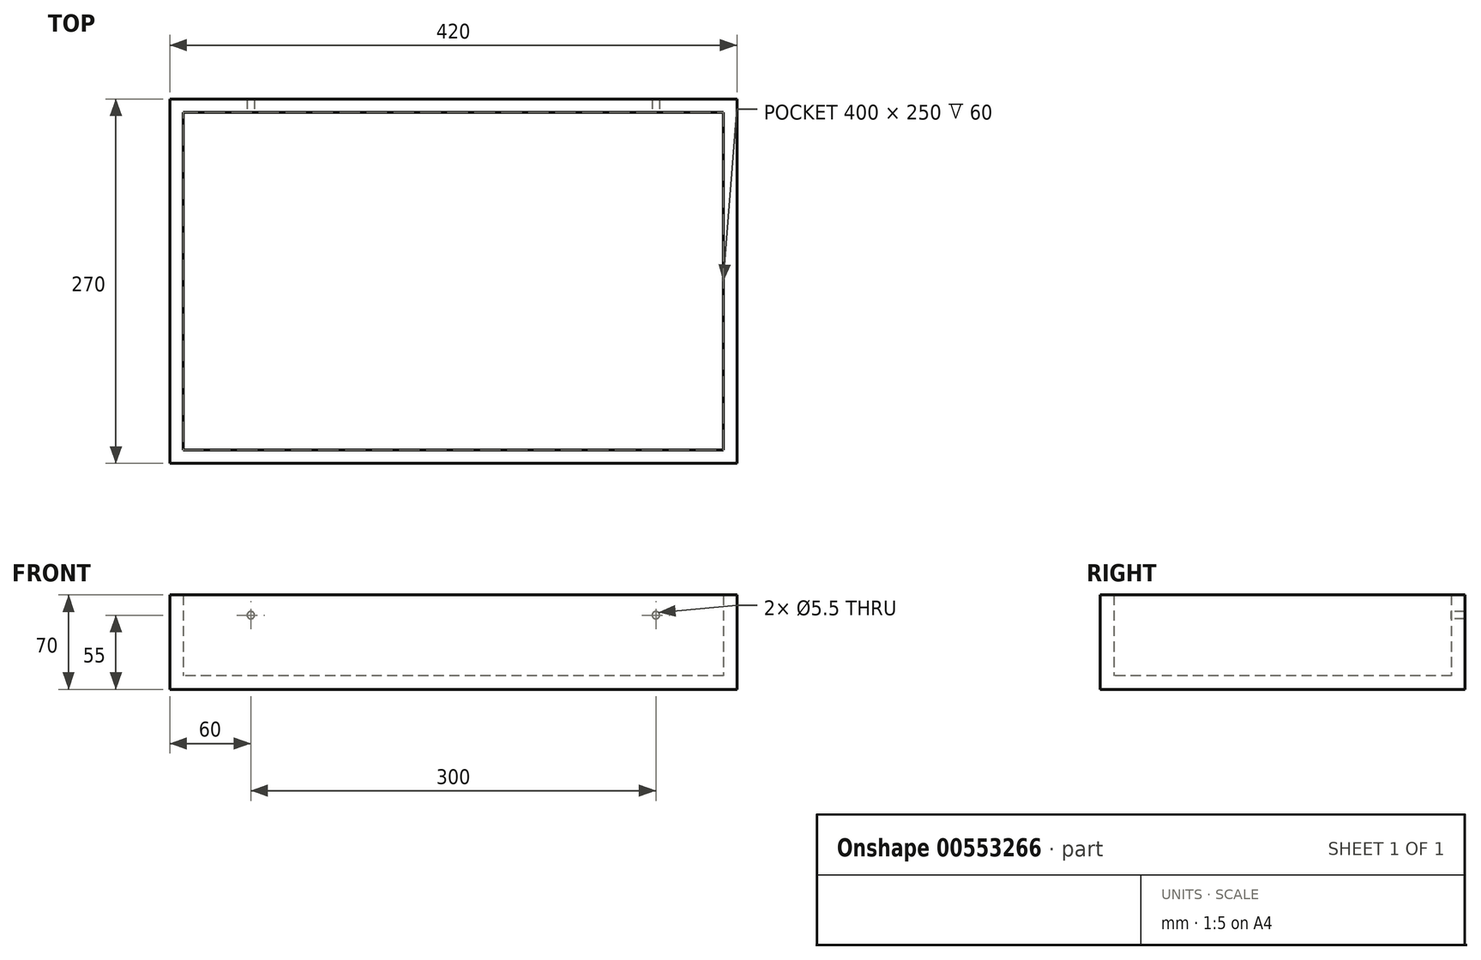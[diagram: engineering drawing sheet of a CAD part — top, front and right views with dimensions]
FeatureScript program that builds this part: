
annotation { "Feature Type Name" : "Feature", "Feature Type Description" : "" }
export const myFeature = defineFeature(function(context is Context, id is Id, definition is map)
    precondition{}
    {
        {
            var Q0;
            Q0=qCreatedBy(makeId("Top.planeOp"),FACE);
            var sketch = newSketch(context, id + "F0", { "sketchPlane" : qUnion([Q0])});
            skLineSegment(sketch, "E0.bottom", {"start": v(200, 125) * mm, "end": v(-200, 125) * mm});
            skLineSegment(sketch, "E0.top", {"start": v(200, -125) * mm, "end": v(-200, -125) * mm});
            skLineSegment(sketch, "E0.left", {"start": v(200, 125) * mm, "end": v(200, -125) * mm});
            skLineSegment(sketch, "E0.right", {"start": v(-200, 125) * mm, "end": v(-200, -125) * mm});
            skPoint(sketch, "E0.middle", {"position": v(0, 0) * mm});
            skSolve(sketch);
        }
        {
            var Q0;
            Q0 = qSketchRegion(id + "F0", true);
            extrude(context, id + "F1", {"entities" : qUnion([Q0]), "depth" : 10 * mm, "offsetDistance" : 25 * mm});
        }
        {
            var Q0;
            Q0=makeQuery(id+"F1.opExtrude","SWEPT_FACE",FACE,{"disambiguationData":[OSD([sQuery(id+"F0.wireOp",EDGE,"E0.left")])]});
            var sketch = newSketch(context, id + "F2", { "sketchPlane" : qUnion([Q0])});
            skLineSegment(sketch, "E1.bottom", {"start": v(-125, 0) * mm, "end": v(125, 0) * mm});
            skLineSegment(sketch, "E1.top", {"start": v(-125, 70) * mm, "end": v(125, 70) * mm});
            skLineSegment(sketch, "E1.left", {"start": v(-125, 0) * mm, "end": v(-125, 70) * mm});
            skLineSegment(sketch, "E1.right", {"start": v(125, 0) * mm, "end": v(125, 70) * mm});
            skSolve(sketch);
        }
        {
            var Q0;
            Q0 = qSketchRegion(id + "F2", true);
            extrude(context, id + "F3", {"entities" : qUnion([Q0]), "operationType" : NewBodyOperationType.ADD, "depth" : 10 * mm, "offsetDistance" : 25 * mm});
        }
        {
            var Q0;
            Q0=makeQuery(id+"F3.boolean.opBoolean","MERGE",FACE,{"derivedFrom":[makeQuery(id+"F1.opExtrude","SWEPT_FACE",FACE,{"disambiguationData":[OSD([sQuery(id+"F0.wireOp",EDGE,"E0.bottom")])]}),makeQuery(id+"F3.opExtrude","SWEPT_FACE",FACE,{"disambiguationData":[OSD([sQuery(id+"F2.wireOp",EDGE,"E1.right")])]})]});
            var sketch = newSketch(context, id + "F4", { "sketchPlane" : qUnion([Q0])});
            skLineSegment(sketch, "E2.bottom", {"start": v(-210, 0) * mm, "end": v(210, 0) * mm});
            skLineSegment(sketch, "E2.top", {"start": v(-210, 70) * mm, "end": v(210, 70) * mm});
            skLineSegment(sketch, "E2.left", {"start": v(-210, 0) * mm, "end": v(-210, 70) * mm});
            skLineSegment(sketch, "E2.right", {"start": v(210, 0) * mm, "end": v(210, 70) * mm});
            skPoint(sketch, "E3", {"position": v(-150, 55) * mm});
            skPoint(sketch, "E4", {"position": v(150, 55) * mm});
            skSolve(sketch);
        }
        {
            var Q0;
            Q0 = qSketchRegion(id + "F4", true);
            extrude(context, id + "F5", {"entities" : qUnion([Q0]), "operationType" : NewBodyOperationType.ADD, "depth" : 10 * mm, "offsetDistance" : 25 * mm});
        }
        {
            var Q0;
            Q0=makeQuery(id+"F1.opExtrude","SWEPT_FACE",FACE,{"disambiguationData":[OSD([sQuery(id+"F0.wireOp",EDGE,"E0.right")])]});
            var sketch = newSketch(context, id + "F6", { "sketchPlane" : qUnion([Q0])});
            skLineSegment(sketch, "E5.bottom", {"start": v(-125, 0) * mm, "end": v(125, 0) * mm});
            skLineSegment(sketch, "E5.top", {"start": v(-125, 70) * mm, "end": v(125, 70) * mm});
            skLineSegment(sketch, "E5.left", {"start": v(-125, 0) * mm, "end": v(-125, 70) * mm});
            skLineSegment(sketch, "E5.right", {"start": v(125, 0) * mm, "end": v(125, 70) * mm});
            skSolve(sketch);
        }
        {
            var Q0;
            Q0 = qSketchRegion(id + "F6", true);
            extrude(context, id + "F7", {"entities" : qUnion([Q0]), "operationType" : NewBodyOperationType.ADD, "depth" : 10 * mm, "offsetDistance" : 25 * mm});
        }
        {
            var Q0;
            Q0=makeQuery(id+"F7.boolean.opBoolean","MERGE",FACE,{"derivedFrom":[makeQuery(id+"F3.boolean.opBoolean","MERGE",FACE,{"derivedFrom":[makeQuery(id+"F1.opExtrude","SWEPT_FACE",FACE,{"disambiguationData":[OSD([sQuery(id+"F0.wireOp",EDGE,"E0.top")])]}),makeQuery(id+"F3.opExtrude","SWEPT_FACE",FACE,{"disambiguationData":[OSD([sQuery(id+"F2.wireOp",EDGE,"E1.left")])]})]}),makeQuery(id+"F7.opExtrude","SWEPT_FACE",FACE,{"disambiguationData":[OSD([sQuery(id+"F6.wireOp",EDGE,"E5.right")])]})]});
            var sketch = newSketch(context, id + "F8", { "sketchPlane" : qUnion([Q0])});
            skLineSegment(sketch, "E6.bottom", {"start": v(-210, 0) * mm, "end": v(210, 0) * mm});
            skLineSegment(sketch, "E6.top", {"start": v(-210, 70) * mm, "end": v(210, 70) * mm});
            skLineSegment(sketch, "E6.left", {"start": v(-210, 0) * mm, "end": v(-210, 70) * mm});
            skLineSegment(sketch, "E6.right", {"start": v(210, 0) * mm, "end": v(210, 70) * mm});
            skSolve(sketch);
        }
        {
            var Q0;
            Q0 = qSketchRegion(id + "F8", true);
            extrude(context, id + "F9", {"entities" : qUnion([Q0]), "operationType" : NewBodyOperationType.ADD, "depth" : 10 * mm, "offsetDistance" : 25 * mm});
        }
        {
            var Q0;
            Q0=sQuery(id+"F4.wireOp",VERTEX,"E3");
            var Q1;
            Q1=makeQuery(id+"F1.opExtrude","SWEPT_BODY",BODY,{"disambiguationData":[OSD([sQuery(id+"F0.wireOp",EDGE,"E0.bottom"),sQuery(id+"F0.wireOp",EDGE,"E0.top"),sQuery(id+"F0.wireOp",EDGE,"E0.left"),sQuery(id+"F0.wireOp",EDGE,"E0.right")])]});
            hole(context, id + "F10", {"style" : HoleStyle.SIMPLE, "endStyle" : HoleEndStyle.THROUGH, "oppositeDirection" : true, "holeDiameter" : 5.5 * mm, "isTappedThrough" : true, "tappedDepth" : 12 * mm, "tapClearance" : 3, "locations" : qUnion([Q0]), "scope" : qUnion([Q1])});
        }
        {
            var Q0;
            Q0=sQuery(id+"F4.wireOp",VERTEX,"E4");
            var Q1;
            Q1=makeQuery(id+"F1.opExtrude","SWEPT_BODY",BODY,{"disambiguationData":[OSD([sQuery(id+"F0.wireOp",EDGE,"E0.bottom"),sQuery(id+"F0.wireOp",EDGE,"E0.top"),sQuery(id+"F0.wireOp",EDGE,"E0.left"),sQuery(id+"F0.wireOp",EDGE,"E0.right")])]});
            hole(context, id + "F11", {"style" : HoleStyle.SIMPLE, "endStyle" : HoleEndStyle.THROUGH, "oppositeDirection" : true, "holeDiameter" : 5.5 * mm, "isTappedThrough" : true, "tappedDepth" : 12 * mm, "tapClearance" : 3, "locations" : qUnion([Q0]), "scope" : qUnion([Q1])});
        }
    });
